# Revit family: Bed_Pan_Cleanser-American_Standard-7866.115.002
name_source: partatom
category: Plumbing Fixtures
units: mm (PartAtom-declared; Revit-internal decimal feet)

## family parameters
Cut with Voids When Loaded = No
Host = Face
OmniClass Number = 23.45.05.14.37
OmniClass Title = Bedpan Washers/Sanitizers
Part Type = Normal
Room Calculation Point = No
Round Connector Dimension = Use Diameter
Shared = Yes

## types (1)
- 7866.115.002
    Assembly Code = D2020100
    Body Material = Cast Brass-American_Standard-002-Chrome_Polished
    CW Connection = Yes
    CWFU = 1.5
    Connection Radius = 1/4"
    Connection Size = 1/2"
    Default Elevation = 0"
    Description = Bed Pan Cleanser with Self-Closing Spray Valve
    HW Connection = Yes
    HWFU = 1.5
    Handle and Lever Material = Rubber-American_Standard-Blue
    Height = 14 7/8"
    Hose Leght = 45 5/8"
    Hose Material = Rubber-American_Standard-Yellow
    Installation Type = Wall Mounted
    Length = 5 3/4"
    Manufacturer = American Standard
    Material = Cast Brass-American_Standard-002-Chrome_Polished
    Model = 7866.115.002
    Product Documentation Link = https://americanstandard.box.com
    Product Page URL = https://www.americanstandard-us.com
    Revised Date = 09/14/2021
    URL = https://www.americanstandard-us.com
    Vent Connection = No
    Waste Connection = No
    Width = 2 5/8"

## geometry (parser evidence)
native form markers: Sweep x2
no freeform markers — native parametric forms only
